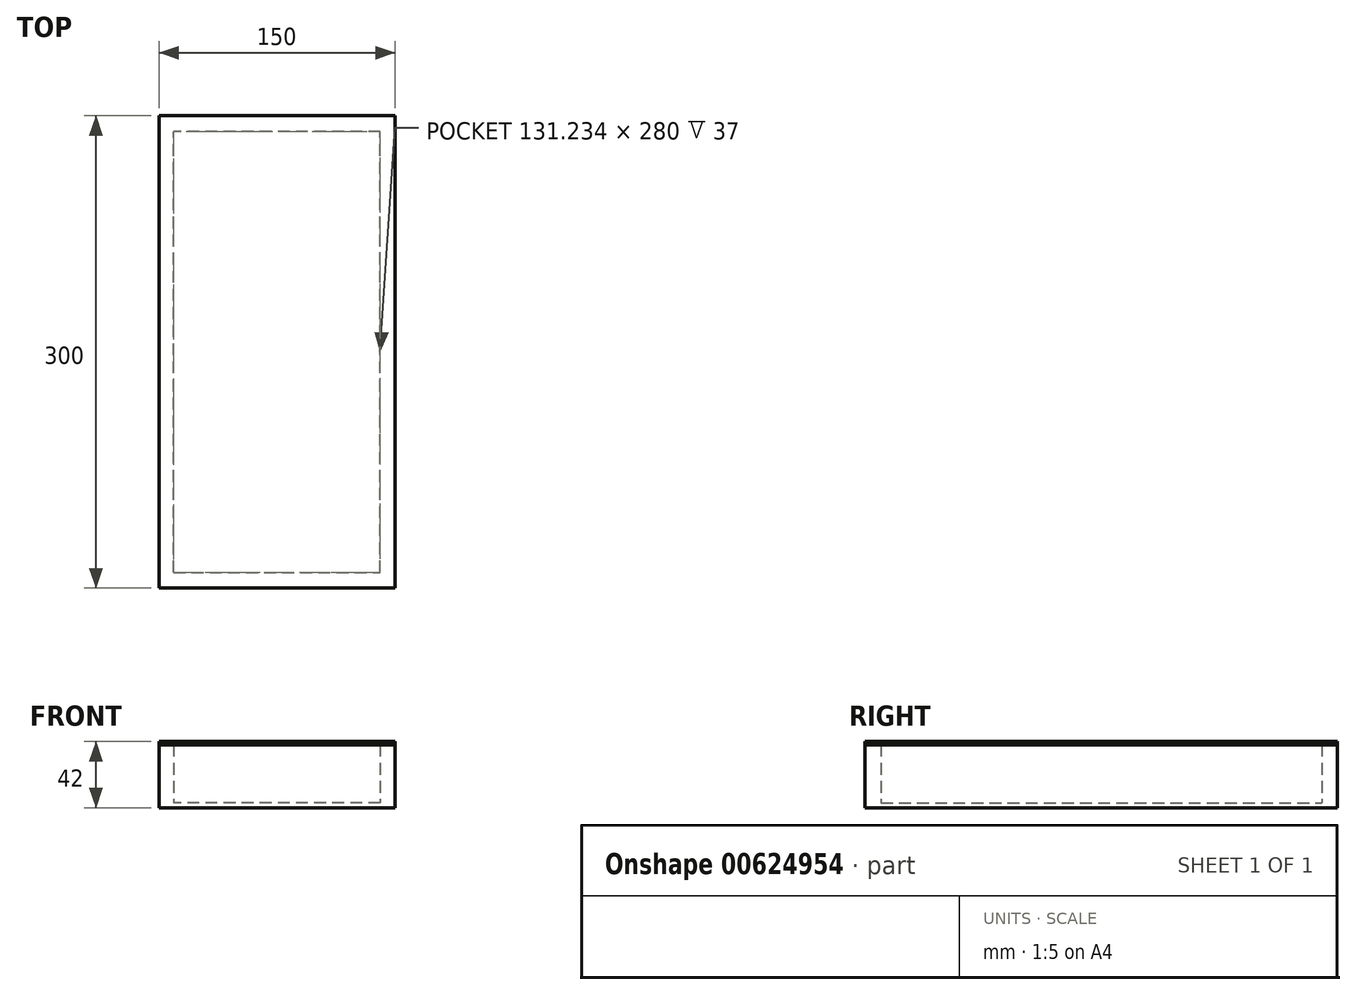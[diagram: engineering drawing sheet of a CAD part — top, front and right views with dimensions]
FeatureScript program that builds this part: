
annotation { "Feature Type Name" : "Feature", "Feature Type Description" : "" }
export const myFeature = defineFeature(function(context is Context, id is Id, definition is map)
    precondition{}
    {
        {
            var Q0;
            Q0=qCreatedBy(makeId("Top.planeOp"),FACE);
            var sketch = newSketch(context, id + "F0", { "sketchPlane" : qUnion([Q0])});
            skLineSegment(sketch, "E0.bottom", {"start": v(75, 150) * mm, "end": v(-75, 150) * mm});
            skLineSegment(sketch, "E0.top", {"start": v(75, -150) * mm, "end": v(-75, -150) * mm});
            skLineSegment(sketch, "E0.left", {"start": v(75, 150) * mm, "end": v(75, -150) * mm});
            skLineSegment(sketch, "E0.right", {"start": v(-75, 150) * mm, "end": v(-75, -150) * mm});
            skPoint(sketch, "E0.middle", {"position": v(0, 0) * mm});
            skSolve(sketch);
        }
        {
            var Q0;
            Q0=qSketchRegion(id+"F0",true);
            extrude(context, id + "F1", {"entities" : qUnion([Q0]), "depth" : 3 * mm, "offsetDistance" : 25.4 * mm});
        }
        {
            var Q0;
            Q0=makeQuery(id+"F1.opExtrude","CAP_FACE",FACE,{"disambiguationData":[OSD([sQuery(id+"F0.wireOp",EDGE,"E0.bottom"),sQuery(id+"F0.wireOp",EDGE,"E0.top"),sQuery(id+"F0.wireOp",EDGE,"E0.left"),sQuery(id+"F0.wireOp",EDGE,"E0.right")])],"isStart":false});
            var sketch = newSketch(context, id + "F2", { "sketchPlane" : qUnion([Q0])});
            skLineSegment(sketch, "E1.bottom", {"start": v(-75, -150) * mm, "end": v(75, -150) * mm});
            skLineSegment(sketch, "E1.top", {"start": v(-75, -140) * mm, "end": v(75, -140) * mm});
            skLineSegment(sketch, "E1.left", {"start": v(-75, -150) * mm, "end": v(-75, -140) * mm});
            skLineSegment(sketch, "E1.right", {"start": v(75, -150) * mm, "end": v(75, -140) * mm});
            skLineSegment(sketch, "E2.bottom", {"start": v(75, -140) * mm, "end": v(65.62, -140) * mm});
            skLineSegment(sketch, "E2.top", {"start": v(75, 140) * mm, "end": v(65.62, 140) * mm});
            skLineSegment(sketch, "E2.left", {"start": v(75, -140) * mm, "end": v(75, 140) * mm});
            skLineSegment(sketch, "E2.right", {"start": v(65.62, -140) * mm, "end": v(65.62, 140) * mm});
            skSolve(sketch);
        }
        {
            var Q0;
            Q0=qSketchRegion(id+"F2",true);
            extrude(context, id + "F3", {"entities" : qUnion([Q0]), "operationType" : NewBodyOperationType.ADD, "depth" : 37 * mm, "offsetDistance" : 25.4 * mm});
        }
        {
            var Q0;
            Q0=makeQuery(id+"F1.opExtrude","SWEPT_BODY",BODY,{"disambiguationData":[OSD([sQuery(id+"F0.wireOp",EDGE,"E0.bottom"),sQuery(id+"F0.wireOp",EDGE,"E0.top"),sQuery(id+"F0.wireOp",EDGE,"E0.left"),sQuery(id+"F0.wireOp",EDGE,"E0.right")])]});
            var Q1;
            Q1=makeQuery(id+"F3.boolean.opBoolean","MERGE",FACE,{"derivedFrom":[makeQuery(id+"F1.opExtrude","SWEPT_FACE",FACE,{"disambiguationData":[OSD([sQuery(id+"F0.wireOp",EDGE,"E0.left")])]}),makeQuery(id+"F3.opExtrude","SWEPT_FACE",FACE,{"disambiguationData":[OSD([sQuery(id+"F2.wireOp",EDGE,"E1.right"),sQuery(id+"F2.wireOp",EDGE,"E2.left")])]})]});
            var Q2;
            Q2=qCreatedBy(makeId("Right.planeOp"),FACE);
            mirror(context, id + "F4", {"operationType" : NewBodyOperationType.ADD, "entities" : qUnion([Q0]), "faces" : qUnion([Q1]), "mirrorPlane" : qUnion([Q2])});
        }
        {
            var Q0;
            Q0=makeQuery(id+"F4.opPattern","COPY",FACE,{"derivedFrom":makeQuery(id+"F3.opExtrude","SWEPT_FACE",FACE,{"disambiguationData":[OSD([sQuery(id+"F2.wireOp",EDGE,"E2.top")])]}),"instanceName":"1"});
            var sketch = newSketch(context, id + "F5", { "sketchPlane" : qUnion([Q0])});
            skLineSegment(sketch, "E3.bottom", {"start": v(-75, 40) * mm, "end": v(75, 40) * mm});
            skLineSegment(sketch, "E3.top", {"start": v(-75, 3) * mm, "end": v(75, 3) * mm});
            skLineSegment(sketch, "E3.left", {"start": v(-75, 40) * mm, "end": v(-75, 3) * mm});
            skLineSegment(sketch, "E3.right", {"start": v(75, 40) * mm, "end": v(75, 3) * mm});
            skSolve(sketch);
        }
        {
            var Q0;
            Q0 = qSketchRegion(id + "F5", true);
            extrude(context, id + "F6", {"entities" : qUnion([Q0]), "operationType" : NewBodyOperationType.ADD, "depth" : 10 * mm, "offsetDistance" : 25.4 * mm});
        }
        {
            var Q0;
            {var subQ0=makeQuery(id+"F3.opExtrude","CAP_FACE",FACE,{"disambiguationData":[OSD([sQuery(id+"F2.wireOp",EDGE,"E1.bottom"),sQuery(id+"F2.wireOp",EDGE,"E1.top"),sQuery(id+"F2.wireOp",EDGE,"E1.left"),sQuery(id+"F2.wireOp",EDGE,"E1.right"),sQuery(id+"F2.wireOp",EDGE,"E2.top"),sQuery(id+"F2.wireOp",EDGE,"E2.left"),sQuery(id+"F2.wireOp",EDGE,"E2.right")])],"isStart":false});Q0=makeQuery(id+"F6.boolean.opBoolean","MERGE",FACE,{"derivedFrom":[makeQuery(id+"F4.boolean.opBoolean","MERGE",FACE,{"derivedFrom":[subQ0,makeQuery(id+"F4.opPattern","COPY",FACE,{"derivedFrom":subQ0,"instanceName":"1"})]}),makeQuery(id+"F6.opExtrude","SWEPT_FACE",FACE,{"disambiguationData":[OSD([sQuery(id+"F5.wireOp",EDGE,"E3.bottom")])]})]});}
            var sketch = newSketch(context, id + "F7", { "sketchPlane" : qUnion([Q0])});
            skLineSegment(sketch, "E4.bottom", {"start": v(-75, 150) * mm, "end": v(75, 150) * mm});
            skLineSegment(sketch, "E4.top", {"start": v(-75, -150) * mm, "end": v(75, -150) * mm});
            skLineSegment(sketch, "E4.left", {"start": v(-75, 150) * mm, "end": v(-75, -150) * mm});
            skLineSegment(sketch, "E4.right", {"start": v(75, 150) * mm, "end": v(75, -150) * mm});
            skSolve(sketch);
        }
        {
            var Q0;
            Q0 = qSketchRegion(id + "F7", true);
            extrude(context, id + "F8", {"entities" : qUnion([Q0]), "depth" : 2 * mm, "offsetDistance" : 25.4 * mm});
        }
    });
